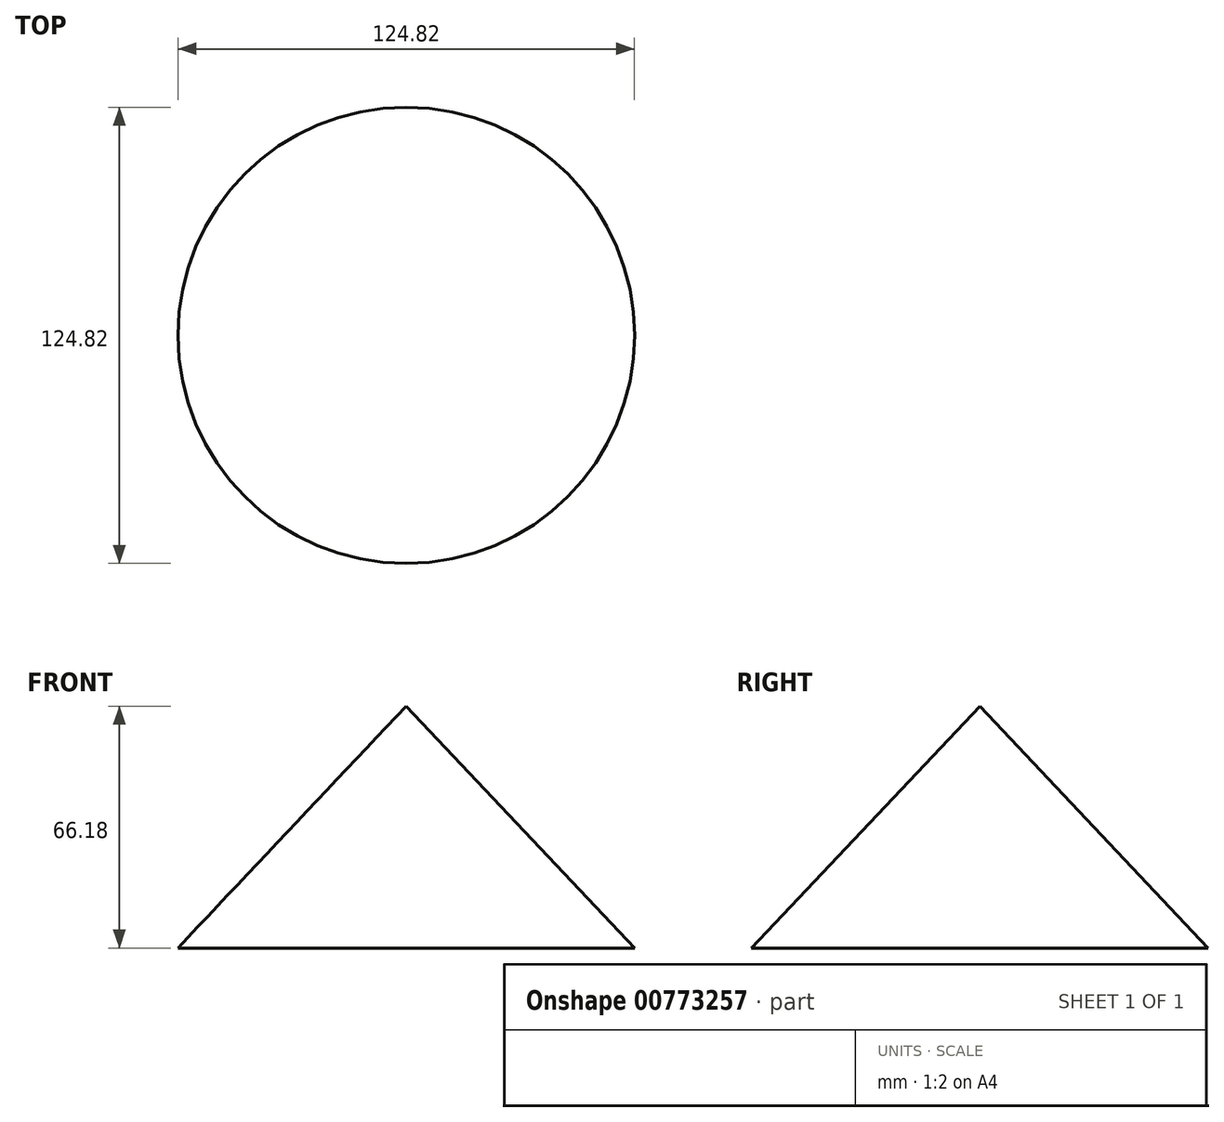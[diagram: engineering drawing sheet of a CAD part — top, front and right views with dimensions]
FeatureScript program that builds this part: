
annotation { "Feature Type Name" : "Feature", "Feature Type Description" : "" }
export const myFeature = defineFeature(function(context is Context, id is Id, definition is map)
    precondition{}
    {
        {
            var Q0;
            Q0=qCreatedBy(makeId("Front.planeOp"),FACE);
            var sketch = newSketch(context, id + "F0", { "sketchPlane" : qUnion([Q0])});
            skLineSegment(sketch, "E0", {"start": v(0, -48.88) * mm, "end": v(0, 33.54) * mm, "construction": true});
            skLineSegment(sketch, "E1", {"start": v(0, -36.25) * mm, "end": v(62.41, -36.25) * mm});
            skLineSegment(sketch, "E2", {"start": v(62.41, -36.25) * mm, "end": v(0, 29.93) * mm});
            skSolve(sketch);
        }
        {
            var Q0;
            Q0=sQuery(id+"F0.wireOp",EDGE,"E1");
            var Q1;
            Q1=sQuery(id+"F0.wireOp",EDGE,"E2");
            var Q2;
            Q2=sQuery(id+"F0.wireOp",EDGE,"E0");
            revolve(context, id + "F1", {"bodyType" : ToolBodyType.SURFACE, "surfaceOperationType" : NewSurfaceOperationType.NEW, "surfaceEntities" : qUnion([Q0, Q1]), "axis" : qUnion([Q2]), "revolveType" : RevolveType.FULL});
        }
    });
